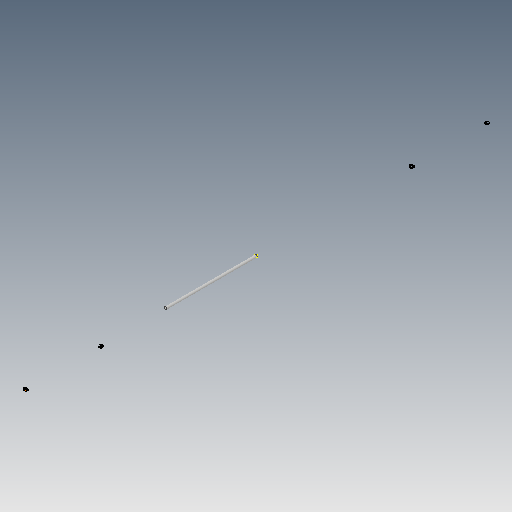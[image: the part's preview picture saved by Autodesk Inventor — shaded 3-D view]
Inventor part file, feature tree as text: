
AUTODESK INVENTOR PART (.ipt)
format: ipt  version: 2017 (Build 210142000, 142)  size: 79,872 bytes
history: native  units: mm
features: sketch x2, extrude x1
ambient origin geometry x8: Origin, YZ Plane, XZ Plane, XY Plane, X Axis, Y Axis, Z Axis, Center Point
bodies: Solid1 (feature_tree)
feature tree (3):
  extrude  "Extrusion1"  Depth=365.0mm TaperAngle=0.0deg
  sketch  "Sketch2"
  sketch  "Sketch1"  dims[d0=10.0mm d1=365.0mm d2=0.0mm]
